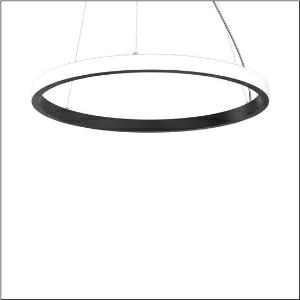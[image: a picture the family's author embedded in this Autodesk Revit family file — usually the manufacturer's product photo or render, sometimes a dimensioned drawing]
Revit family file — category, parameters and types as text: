
# Revit family: silica_r__21_ring-o_5pjbo4d3104a_8b26
name_source: partatom
category: Lighting Fixtures
units: mm (PartAtom-declared; Revit-internal decimal feet)

## family parameters
Cut with Voids When Loaded = No
Host = Face
Light Source = No
Part Type = Normal
Room Calculation Point = No
Round Connector Dimension = Use Diameter
Shared = No

## types (1)
- Silica® 21 Ring-O (1 x LED, 9260 lm, 140 W, 4000K)
    Apparent Load = 140 VA
    CIE Flux Codes = 2 16 49 50 100
    Color Rendering = 80
    Color Temperature = 4000K
    Default Elevation = 1800 mm
    Description = Silica® 21 Ring-O, suspended luminaire, of PMMA, frosted, light emission: outer ring side luminous distribution, primary light characteristic: symmetric, installation type: suspended mounting, LED, rated luminous flux: 9.260lm, luminous efficacy: 66lm/W, light colour: 840, colour temperature: 4000K, with terminal, 5-pole, mains connection: 230V, AC/DC, 0/50..60Hz, rated input power: 140W, housing, of extruded aluminium section, jet black (RAL 9005), diameter: 1.480mm, ceiling canopy, jet black (RAL 9005), protection rating (lamp compartment): IP40, insulation class (complete): insulation class I (protective earthing), certification: CE, impact resistance: IK02, permissible operating ambient temperature: 0..+35°C, packaging unit: 1 piece
    Height = 48 mm  [stored 0.15748 ft]
    Lamp = 1 x LED
    Lamp Light Flux = 9260 lm
    Lamp Power = 140 W
    Lamp count = 1
    Length = 1480 mm
    Luminous efficacy = 66 lm/W
    Manufacturer = Siteco
    ModVariant = No
    Model = 5PJBO4D3104A
    Mounting Place = Ceiling
    Mounting Type = Pendant
    Number of Poles = 1
    OnlyDefault = Yes
    Power Factor = 1
    Product Name = Silica® 21 Ring-O
    Product group = suspended luminaire
    ProductGroupID = 904
    Protection Class = Protection class I
    Protection Degree = IP 40
    RLX_Detail_Level = 1
    RLX_Emergency_Light_Flux = 0 lm
    RLX_Emergency_Type = 0
    RLX_Emergency_Type_DB = No
    RlxData = <blob elided: 20537 chars, md5=36447c11>
    Socket = socket
    Standby Power = 0 W
    System Light Flux = 9260 lm
    System Power = 140 W
    Type Comments = Product without accessories
    Type Image = l_1258389.jpg
    URL = http://relux.com
    VarID = ---
    Voltage = 0 V
    Weight = 0.00 kg
    Width = 0 mm  [stored 0 ft]

note: [stored X ft] marks values corroborated as IEEE doubles in the binary element streams (Revit-internal decimal feet)

## geometry (parser evidence)
native form markers: Blend x4, Sweep x16
no freeform markers — native parametric forms only
